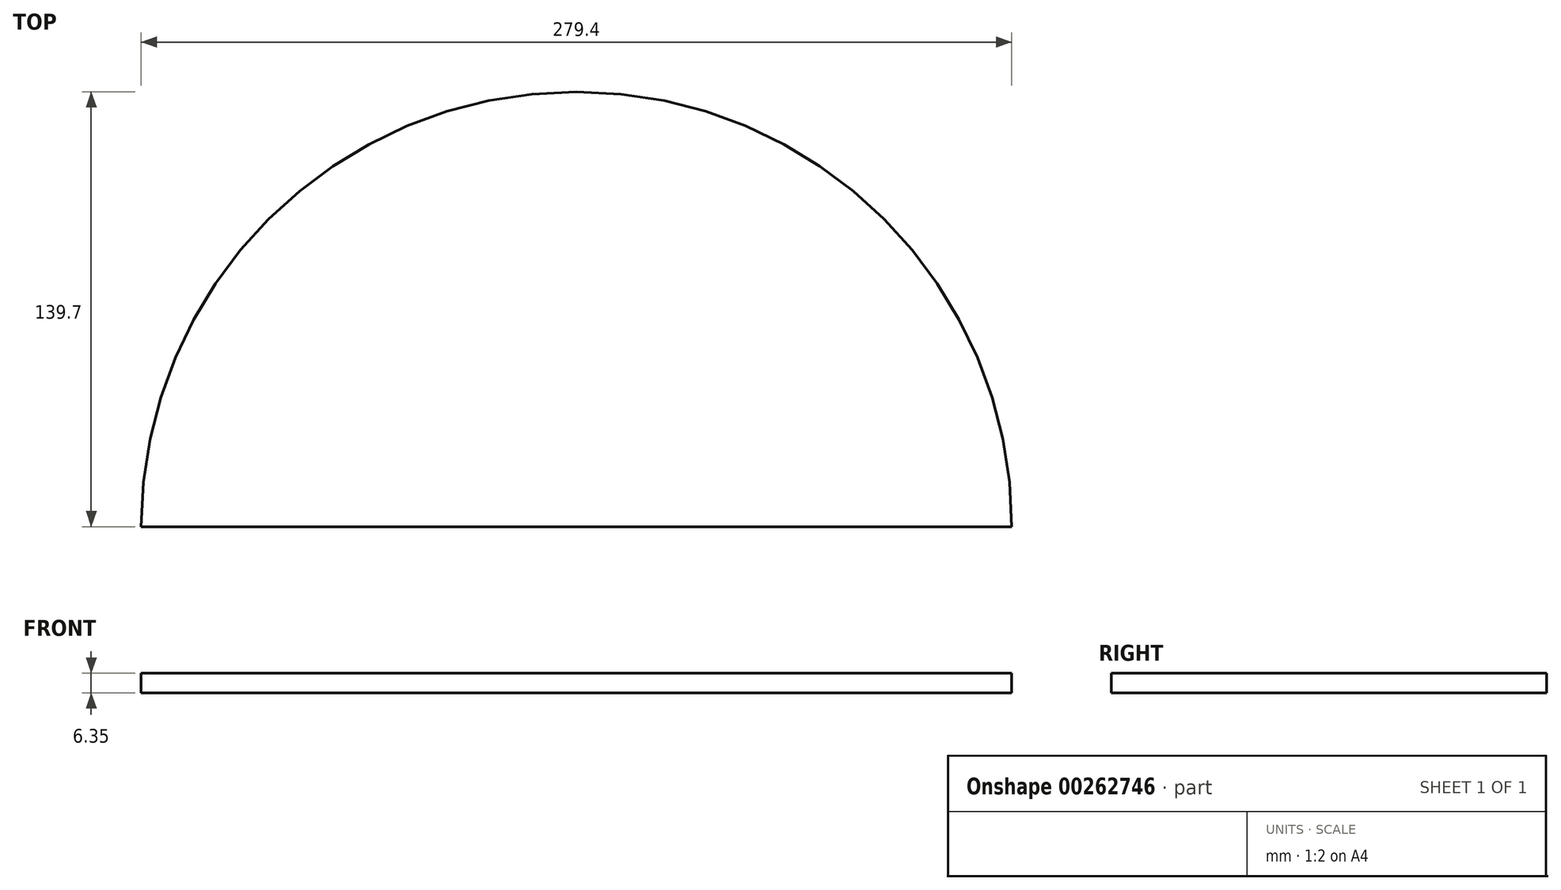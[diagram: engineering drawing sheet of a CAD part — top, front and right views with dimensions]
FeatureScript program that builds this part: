
annotation { "Feature Type Name" : "Feature", "Feature Type Description" : "" }
export const myFeature = defineFeature(function(context is Context, id is Id, definition is map)
    precondition{}
    {
        {
            var Q0;
            Q0=qCreatedBy(makeId("Top.planeOp"),FACE);
            var sketch = newSketch(context, id + "F0", { "sketchPlane" : qUnion([Q0])});
            skArc(sketch, "E0", {"start": v(139.7, 0) * mm, "mid": v(0, 139.7) * mm, "end": v(-139.7, 0) * mm});
            skLineSegment(sketch, "E1", {"start": v(-139.7, 0) * mm, "end": v(139.7, 0) * mm});
            skSolve(sketch);
        }
        {
            var Q0;
            Q0=makeQuery(id+"F0.imprint","IMPRINT",FACE,{"disambiguationData":[TD([[makeQuery(id+"F0.imprint","IMPRINT",EDGE,{"derivedFrom":sQuery(id+"F0.wireOp",EDGE,"E0")}),1.0]])]});
            extrude(context, id + "F1", {"entities" : qUnion([Q0]), "depth" : 6.35 * mm});
        }
    });
